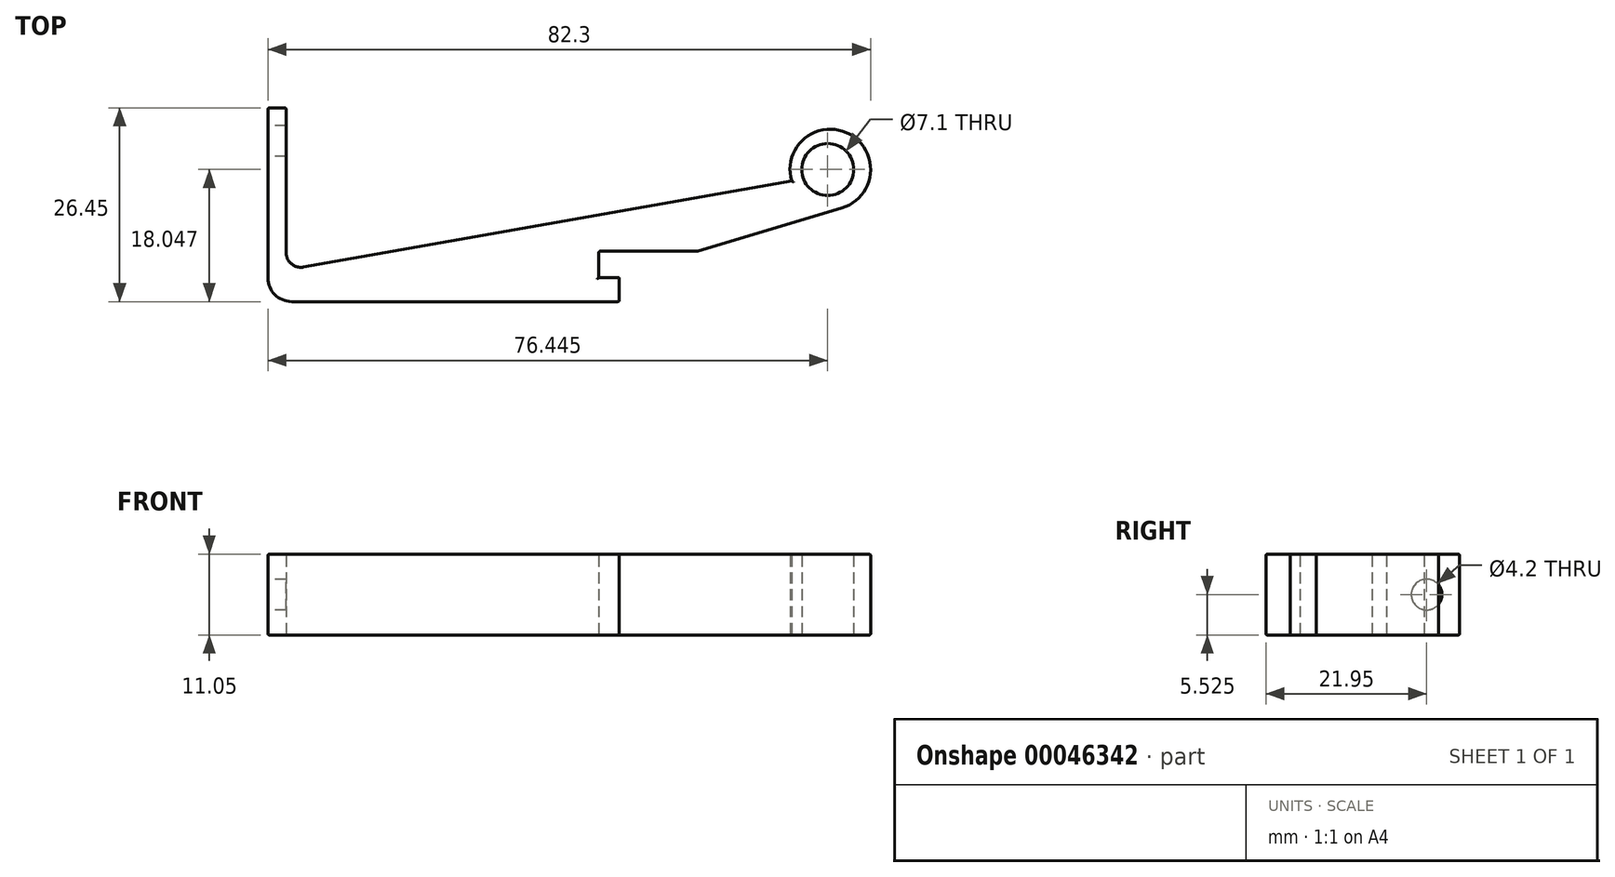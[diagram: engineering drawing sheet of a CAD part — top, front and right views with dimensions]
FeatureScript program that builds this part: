
annotation { "Feature Type Name" : "Feature", "Feature Type Description" : "" }
export const myFeature = defineFeature(function(context is Context, id is Id, definition is map)
    precondition{}
    {
        {
            var Q0;
            Q0=qCreatedBy(makeId("Top.planeOp"),FACE);
            var sketch = newSketch(context, id + "F0", { "sketchPlane" : qUnion([Q0])});
            skLineSegment(sketch, "E0.bottom", {"start": v(-32.06, 26.45) * mm, "end": v(-29.56, 26.45) * mm});
            skLineSegment(sketch, "E0.top", {"start": v(-32.06, 0) * mm, "end": v(-29.56, 0) * mm});
            skLineSegment(sketch, "E0.left", {"start": v(-32.06, 26.45) * mm, "end": v(-32.06, 0) * mm});
            skLineSegment(sketch, "E0.right", {"start": v(-29.56, 26.45) * mm, "end": v(-29.56, 4.3) * mm});
            skLineSegment(sketch, "E1", {"start": v(-29.56, 0) * mm, "end": v(15.94, 0) * mm});
            skLineSegment(sketch, "E2", {"start": v(15.94, 0) * mm, "end": v(15.94, 3.3) * mm});
            skLineSegment(sketch, "E3", {"start": v(15.94, 3.3) * mm, "end": v(13.14, 3.3) * mm});
            skLineSegment(sketch, "E4", {"start": v(13.14, 3.3) * mm, "end": v(13.14, 6.9) * mm});
            skLineSegment(sketch, "E5", {"start": v(13.14, 6.9) * mm, "end": v(26.64, 6.9) * mm});
            skLineSegment(sketch, "E6", {"start": v(26.64, 6.9) * mm, "end": v(46.32, 12.77) * mm});
            skLineSegment(sketch, "E7", {"start": v(39.47, 16.47) * mm, "end": v(-29.56, 4.3) * mm});
            skLineSegment(sketch, "E8", {"start": v(-47.11, 0) * mm, "end": v(50.52, 0) * mm, "construction": true});
            skLineSegment(sketch, "E9", {"start": v(19.89, 6.9) * mm, "end": v(93.74, 6.9) * mm, "construction": true});
            skArc(sketch, "E10", {"start": v(46.32, 12.77) * mm, "mid": v(47.36, 22.88) * mm, "end": v(39.47, 16.47) * mm});
            skCircle(sketch, "E11", {"center": v(44.39, 18.05) * mm, "radius": 3.55 * mm});
            skPoint(sketch, "E12.end.orphan", {"position": v(40.88, 17.5) * mm});
            skPoint(sketch, "E13.start.orphan", {"position": v(50.24, 18.04) * mm});
            skPoint(sketch, "E14.end.orphan", {"position": v(13.14, 11.83) * mm});
            skPoint(sketch, "E15.end.orphan", {"position": v(26.64, 14.2) * mm});
            skPoint(sketch, "E16.orphan", {"position": v(53.1, 18.05) * mm});
            skPoint(sketch, "E17.orphan", {"position": v(44.39, 24.3) * mm});
            skPoint(sketch, "E18.end.orphan", {"position": v(44.39, 21.6) * mm});
            skPoint(sketch, "E18.start.orphan", {"position": v(44.39, 23.53) * mm});
            skPoint(sketch, "E19.end.orphan", {"position": v(47.94, 18.05) * mm});
            skPoint(sketch, "E20.trimOffspring.end.orphan", {"position": v(39.24, 18.05) * mm});
            skPoint(sketch, "E20.trimOffspring.start.orphan", {"position": v(40.84, 18.05) * mm});
            skPoint(sketch, "E21.trimOffspring.end.orphan", {"position": v(44.39, 12.2) * mm});
            skPoint(sketch, "E21.trimOffspring.start.orphan", {"position": v(44.39, 14.5) * mm});
            skSolve(sketch);
        }
        {
            var Q0;
            Q0=makeQuery(id+"F0.imprint","IMPRINT",FACE,{"disambiguationData":[TD([[makeQuery(id+"F0.imprint","IMPRINT",EDGE,{"derivedFrom":sQuery(id+"F0.wireOp",EDGE,"E0.bottom")}),-1.0]])]});
            extrude(context, id + "F1", {"entities" : qUnion([Q0]), "depth" : 11.05 * mm});
        }
        {
            var Q0;
            Q0=makeQuery(id+"F1.opExtrude","SWEPT_EDGE",EDGE,{"disambiguationData":[OSD([sQuery(id+"F0.wireOp",EDGE,"E0.top"),sQuery(id+"F0.wireOp",EDGE,"E0.left")])]});
            fillet(context, id + "F2", {"entities" : qUnion([Q0]), "radius" : 3.25 * mm, "tangentPropagation" : true, "allowEdgeOverflow" : false});
        }
        {
            var Q0;
            Q0=makeQuery(id+"F1.opExtrude","SWEPT_EDGE",EDGE,{"disambiguationData":[OSD([sQuery(id+"F0.wireOp",EDGE,"E0.right"),sQuery(id+"F0.wireOp",EDGE,"E7")])]});
            fillet(context, id + "F3", {"entities" : qUnion([Q0]), "radius" : 2 * mm, "tangentPropagation" : true, "allowEdgeOverflow" : false});
        }
        {
            var Q0;
            Q0=makeQuery(id+"F1.opExtrude","CAP_EDGE",EDGE,{"disambiguationData":[OSD([sQuery(id+"F0.wireOp",EDGE,"E7")])],"isStart":true});
            var Q1;
            Q1=makeQuery(id+"F1.opExtrude","CAP_EDGE",EDGE,{"disambiguationData":[OSD([sQuery(id+"F0.wireOp",EDGE,"E10")])],"isStart":true});
            var Q2;
            Q2=makeQuery(id+"F1.opExtrude","CAP_EDGE",EDGE,{"disambiguationData":[OSD([sQuery(id+"F0.wireOp",EDGE,"E6")])],"isStart":true});
            var Q3;
            Q3=makeQuery(id+"F1.opExtrude","CAP_EDGE",EDGE,{"disambiguationData":[OSD([sQuery(id+"F0.wireOp",EDGE,"E5")])],"isStart":true});
            var Q4;
            Q4=makeQuery(id+"F1.opExtrude","CAP_EDGE",EDGE,{"disambiguationData":[OSD([sQuery(id+"F0.wireOp",EDGE,"E4")])],"isStart":true});
            var Q5;
            Q5=makeQuery(id+"F1.opExtrude","CAP_EDGE",EDGE,{"disambiguationData":[OSD([sQuery(id+"F0.wireOp",EDGE,"E3")])],"isStart":true});
            var Q6;
            Q6=makeQuery(id+"F1.opExtrude","CAP_EDGE",EDGE,{"disambiguationData":[OSD([sQuery(id+"F0.wireOp",EDGE,"E0.top"),sQuery(id+"F0.wireOp",EDGE,"E1")])],"isStart":true});
            var Q7;
            Q7=makeQuery(id+"F1.opExtrude","CAP_EDGE",EDGE,{"disambiguationData":[OSD([sQuery(id+"F0.wireOp",EDGE,"E2")])],"isStart":true});
            var Q8;
            {var subQ0=sQuery(id+"F0.wireOp",EDGE,"E0.top");var subQ1=sQuery(id+"F0.wireOp",EDGE,"E0.left");Q8=makeQuery(id+"F2.opFillet","BLEND_EDGE",EDGE,{"blendedFrom":[makeQuery(id+"F1.opExtrude","SWEPT_EDGE",EDGE,{"disambiguationData":[OSD([subQ0,subQ1])]}),makeQuery(id+"F1.opExtrude","CAP_FACE",FACE,{"disambiguationData":[OSD([sQuery(id+"F0.wireOp",EDGE,"E0.bottom"),subQ0,subQ1,sQuery(id+"F0.wireOp",EDGE,"E0.right"),sQuery(id+"F0.wireOp",EDGE,"E1"),sQuery(id+"F0.wireOp",EDGE,"E2"),sQuery(id+"F0.wireOp",EDGE,"E3"),sQuery(id+"F0.wireOp",EDGE,"E4"),sQuery(id+"F0.wireOp",EDGE,"E5"),sQuery(id+"F0.wireOp",EDGE,"E6"),sQuery(id+"F0.wireOp",EDGE,"E7"),sQuery(id+"F0.wireOp",EDGE,"E10"),sQuery(id+"F0.wireOp",EDGE,"E11")])],"isStart":true})],"blendedInto":[makeQuery(id+"F1.opExtrude","CAP_FACE",FACE,{"disambiguationData":[OSD([sQuery(id+"F0.wireOp",EDGE,"E0.bottom"),subQ0,subQ1,sQuery(id+"F0.wireOp",EDGE,"E0.right"),sQuery(id+"F0.wireOp",EDGE,"E1"),sQuery(id+"F0.wireOp",EDGE,"E2"),sQuery(id+"F0.wireOp",EDGE,"E3"),sQuery(id+"F0.wireOp",EDGE,"E4"),sQuery(id+"F0.wireOp",EDGE,"E5"),sQuery(id+"F0.wireOp",EDGE,"E6"),sQuery(id+"F0.wireOp",EDGE,"E7"),sQuery(id+"F0.wireOp",EDGE,"E10"),sQuery(id+"F0.wireOp",EDGE,"E11")])],"isStart":true})]});}
            var Q9;
            {var subQ0=sQuery(id+"F0.wireOp",EDGE,"E0.right");var subQ1=sQuery(id+"F0.wireOp",EDGE,"E7");Q9=makeQuery(id+"F3.opFillet","BLEND_EDGE",EDGE,{"blendedFrom":[makeQuery(id+"F1.opExtrude","SWEPT_EDGE",EDGE,{"disambiguationData":[OSD([subQ0,subQ1])]}),makeQuery(id+"F1.opExtrude","CAP_FACE",FACE,{"disambiguationData":[OSD([sQuery(id+"F0.wireOp",EDGE,"E0.bottom"),sQuery(id+"F0.wireOp",EDGE,"E0.top"),sQuery(id+"F0.wireOp",EDGE,"E0.left"),subQ0,sQuery(id+"F0.wireOp",EDGE,"E1"),sQuery(id+"F0.wireOp",EDGE,"E2"),sQuery(id+"F0.wireOp",EDGE,"E3"),sQuery(id+"F0.wireOp",EDGE,"E4"),sQuery(id+"F0.wireOp",EDGE,"E5"),sQuery(id+"F0.wireOp",EDGE,"E6"),subQ1,sQuery(id+"F0.wireOp",EDGE,"E10"),sQuery(id+"F0.wireOp",EDGE,"E11")])],"isStart":true})],"blendedInto":[makeQuery(id+"F1.opExtrude","CAP_FACE",FACE,{"disambiguationData":[OSD([sQuery(id+"F0.wireOp",EDGE,"E0.bottom"),sQuery(id+"F0.wireOp",EDGE,"E0.top"),sQuery(id+"F0.wireOp",EDGE,"E0.left"),subQ0,sQuery(id+"F0.wireOp",EDGE,"E1"),sQuery(id+"F0.wireOp",EDGE,"E2"),sQuery(id+"F0.wireOp",EDGE,"E3"),sQuery(id+"F0.wireOp",EDGE,"E4"),sQuery(id+"F0.wireOp",EDGE,"E5"),sQuery(id+"F0.wireOp",EDGE,"E6"),subQ1,sQuery(id+"F0.wireOp",EDGE,"E10"),sQuery(id+"F0.wireOp",EDGE,"E11")])],"isStart":true})]});}
            var Q10;
            Q10=makeQuery(id+"F1.opExtrude","CAP_EDGE",EDGE,{"disambiguationData":[OSD([sQuery(id+"F0.wireOp",EDGE,"E0.right")])],"isStart":true});
            var Q11;
            Q11=makeQuery(id+"F1.opExtrude","CAP_EDGE",EDGE,{"disambiguationData":[OSD([sQuery(id+"F0.wireOp",EDGE,"E0.left")])],"isStart":true});
            var Q12;
            Q12=makeQuery(id+"F1.opExtrude","SWEPT_EDGE",EDGE,{"disambiguationData":[OSD([sQuery(id+"F0.wireOp",EDGE,"E0.bottom"),sQuery(id+"F0.wireOp",EDGE,"E0.left")])]});
            var Q13;
            Q13=makeQuery(id+"F1.opExtrude","SWEPT_EDGE",EDGE,{"disambiguationData":[OSD([sQuery(id+"F0.wireOp",EDGE,"E0.bottom"),sQuery(id+"F0.wireOp",EDGE,"E0.right")])]});
            var Q14;
            Q14=makeQuery(id+"F1.opExtrude","CAP_EDGE",EDGE,{"disambiguationData":[OSD([sQuery(id+"F0.wireOp",EDGE,"E0.bottom")])],"isStart":false});
            var Q15;
            Q15=makeQuery(id+"F1.opExtrude","CAP_EDGE",EDGE,{"disambiguationData":[OSD([sQuery(id+"F0.wireOp",EDGE,"E0.left")])],"isStart":false});
            var Q16;
            Q16=makeQuery(id+"F1.opExtrude","CAP_EDGE",EDGE,{"disambiguationData":[OSD([sQuery(id+"F0.wireOp",EDGE,"E0.right")])],"isStart":false});
            var Q17;
            {var subQ0=sQuery(id+"F0.wireOp",EDGE,"E0.top");var subQ1=sQuery(id+"F0.wireOp",EDGE,"E0.left");Q17=makeQuery(id+"F2.opFillet","BLEND_EDGE",EDGE,{"blendedFrom":[makeQuery(id+"F1.opExtrude","SWEPT_EDGE",EDGE,{"disambiguationData":[OSD([subQ0,subQ1])]}),makeQuery(id+"F1.opExtrude","CAP_FACE",FACE,{"disambiguationData":[OSD([sQuery(id+"F0.wireOp",EDGE,"E0.bottom"),subQ0,subQ1,sQuery(id+"F0.wireOp",EDGE,"E0.right"),sQuery(id+"F0.wireOp",EDGE,"E1"),sQuery(id+"F0.wireOp",EDGE,"E2"),sQuery(id+"F0.wireOp",EDGE,"E3"),sQuery(id+"F0.wireOp",EDGE,"E4"),sQuery(id+"F0.wireOp",EDGE,"E5"),sQuery(id+"F0.wireOp",EDGE,"E6"),sQuery(id+"F0.wireOp",EDGE,"E7"),sQuery(id+"F0.wireOp",EDGE,"E10"),sQuery(id+"F0.wireOp",EDGE,"E11")])],"isStart":false})],"blendedInto":[makeQuery(id+"F1.opExtrude","CAP_FACE",FACE,{"disambiguationData":[OSD([sQuery(id+"F0.wireOp",EDGE,"E0.bottom"),subQ0,subQ1,sQuery(id+"F0.wireOp",EDGE,"E0.right"),sQuery(id+"F0.wireOp",EDGE,"E1"),sQuery(id+"F0.wireOp",EDGE,"E2"),sQuery(id+"F0.wireOp",EDGE,"E3"),sQuery(id+"F0.wireOp",EDGE,"E4"),sQuery(id+"F0.wireOp",EDGE,"E5"),sQuery(id+"F0.wireOp",EDGE,"E6"),sQuery(id+"F0.wireOp",EDGE,"E7"),sQuery(id+"F0.wireOp",EDGE,"E10"),sQuery(id+"F0.wireOp",EDGE,"E11")])],"isStart":false})]});}
            var Q18;
            {var subQ0=sQuery(id+"F0.wireOp",EDGE,"E0.right");var subQ1=sQuery(id+"F0.wireOp",EDGE,"E7");Q18=makeQuery(id+"F3.opFillet","BLEND_EDGE",EDGE,{"blendedFrom":[makeQuery(id+"F1.opExtrude","SWEPT_EDGE",EDGE,{"disambiguationData":[OSD([subQ0,subQ1])]}),makeQuery(id+"F1.opExtrude","CAP_FACE",FACE,{"disambiguationData":[OSD([sQuery(id+"F0.wireOp",EDGE,"E0.bottom"),sQuery(id+"F0.wireOp",EDGE,"E0.top"),sQuery(id+"F0.wireOp",EDGE,"E0.left"),subQ0,sQuery(id+"F0.wireOp",EDGE,"E1"),sQuery(id+"F0.wireOp",EDGE,"E2"),sQuery(id+"F0.wireOp",EDGE,"E3"),sQuery(id+"F0.wireOp",EDGE,"E4"),sQuery(id+"F0.wireOp",EDGE,"E5"),sQuery(id+"F0.wireOp",EDGE,"E6"),subQ1,sQuery(id+"F0.wireOp",EDGE,"E10"),sQuery(id+"F0.wireOp",EDGE,"E11")])],"isStart":false})],"blendedInto":[makeQuery(id+"F1.opExtrude","CAP_FACE",FACE,{"disambiguationData":[OSD([sQuery(id+"F0.wireOp",EDGE,"E0.bottom"),sQuery(id+"F0.wireOp",EDGE,"E0.top"),sQuery(id+"F0.wireOp",EDGE,"E0.left"),subQ0,sQuery(id+"F0.wireOp",EDGE,"E1"),sQuery(id+"F0.wireOp",EDGE,"E2"),sQuery(id+"F0.wireOp",EDGE,"E3"),sQuery(id+"F0.wireOp",EDGE,"E4"),sQuery(id+"F0.wireOp",EDGE,"E5"),sQuery(id+"F0.wireOp",EDGE,"E6"),subQ1,sQuery(id+"F0.wireOp",EDGE,"E10"),sQuery(id+"F0.wireOp",EDGE,"E11")])],"isStart":false})]});}
            var Q19;
            Q19=makeQuery(id+"F1.opExtrude","CAP_EDGE",EDGE,{"disambiguationData":[OSD([sQuery(id+"F0.wireOp",EDGE,"E0.top"),sQuery(id+"F0.wireOp",EDGE,"E1")])],"isStart":false});
            var Q20;
            Q20=makeQuery(id+"F1.opExtrude","CAP_EDGE",EDGE,{"disambiguationData":[OSD([sQuery(id+"F0.wireOp",EDGE,"E7")])],"isStart":false});
            var Q21;
            Q21=makeQuery(id+"F1.opExtrude","CAP_EDGE",EDGE,{"disambiguationData":[OSD([sQuery(id+"F0.wireOp",EDGE,"E2")])],"isStart":false});
            var Q22;
            Q22=makeQuery(id+"F1.opExtrude","CAP_EDGE",EDGE,{"disambiguationData":[OSD([sQuery(id+"F0.wireOp",EDGE,"E5")])],"isStart":false});
            var Q23;
            Q23=makeQuery(id+"F1.opExtrude","CAP_EDGE",EDGE,{"disambiguationData":[OSD([sQuery(id+"F0.wireOp",EDGE,"E6")])],"isStart":false});
            var Q24;
            Q24=makeQuery(id+"F1.opExtrude","CAP_EDGE",EDGE,{"disambiguationData":[OSD([sQuery(id+"F0.wireOp",EDGE,"E10")])],"isStart":false});
            var Q25;
            Q25=makeQuery(id+"F1.opExtrude","CAP_EDGE",EDGE,{"disambiguationData":[OSD([sQuery(id+"F0.wireOp",EDGE,"E3")])],"isStart":false});
            var Q26;
            Q26=makeQuery(id+"F1.opExtrude","SWEPT_EDGE",EDGE,{"disambiguationData":[OSD([sQuery(id+"F0.wireOp",EDGE,"E2"),sQuery(id+"F0.wireOp",EDGE,"E3")])]});
            var Q27;
            Q27=makeQuery(id+"F1.opExtrude","CAP_EDGE",EDGE,{"disambiguationData":[OSD([sQuery(id+"F0.wireOp",EDGE,"E4")])],"isStart":false});
            var Q28;
            Q28=makeQuery(id+"F1.opExtrude","SWEPT_EDGE",EDGE,{"disambiguationData":[OSD([sQuery(id+"F0.wireOp",EDGE,"E4"),sQuery(id+"F0.wireOp",EDGE,"E5")])]});
            var Q29;
            Q29=makeQuery(id+"F1.opExtrude","SWEPT_EDGE",EDGE,{"disambiguationData":[OSD([sQuery(id+"F0.wireOp",EDGE,"E1"),sQuery(id+"F0.wireOp",EDGE,"E2")])]});
            var Q30;
            Q30=makeQuery(id+"F1.opExtrude","SWEPT_EDGE",EDGE,{"disambiguationData":[OSD([sQuery(id+"F0.wireOp",EDGE,"E5"),sQuery(id+"F0.wireOp",EDGE,"E6")])]});
            var Q31;
            Q31=makeQuery(id+"F1.opExtrude","CAP_EDGE",EDGE,{"disambiguationData":[OSD([sQuery(id+"F0.wireOp",EDGE,"E11")])],"isStart":false});
            var Q32;
            Q32=makeQuery(id+"F1.opExtrude","CAP_EDGE",EDGE,{"disambiguationData":[OSD([sQuery(id+"F0.wireOp",EDGE,"E11")])],"isStart":true});
            var Q33;
            Q33=makeQuery(id+"F1.opExtrude","CAP_EDGE",EDGE,{"disambiguationData":[OSD([sQuery(id+"F0.wireOp",EDGE,"E0.bottom")])],"isStart":true});
            fillet(context, id + "F4", {"entities" : qUnion([Q0, Q1, Q2, Q3, Q4, Q5, Q6, Q7, Q8, Q9, Q10, Q11, Q12, Q13, Q14, Q15, Q16, Q17, Q18, Q19, Q20, Q21, Q22, Q23, Q24, Q25, Q26, Q27, Q28, Q29, Q30, Q31, Q32, Q33]), "radius" : 0.2 * mm, "tangentPropagation" : true, "allowEdgeOverflow" : false});
        }
        {
            var Q0;
            Q0=makeQuery(id+"F1.opExtrude","SWEPT_FACE",FACE,{"disambiguationData":[OSD([sQuery(id+"F0.wireOp",EDGE,"E0.left")])]});
            var sketch = newSketch(context, id + "F5", { "sketchPlane" : qUnion([Q0])});
            skCircle(sketch, "E22", {"center": v(-21.95, 5.53) * mm, "radius": 2.1 * mm});
            skLineSegment(sketch, "E23", {"start": v(-24.48, 0) * mm, "end": v(-2.12, 0) * mm, "construction": true});
            skLineSegment(sketch, "E24", {"start": v(-34.74, 0) * mm, "end": v(2.18, 0) * mm, "construction": true});
            skLineSegment(sketch, "E25", {"start": v(0, 11.05) * mm, "end": v(-36.1, 11.05) * mm, "construction": true});
            skSolve(sketch);
        }
        {
            var Q0;
            Q0=makeQuery(id+"F5.imprint","IMPRINT",FACE,{"disambiguationData":[TD([[makeQuery(id+"F5.imprint","IMPRINT",EDGE,{"derivedFrom":sQuery(id+"F5.wireOp",EDGE,"E22")}),1.0]])]});
            extrude(context, id + "F6", {"entities" : qUnion([Q0]), "operationType" : NewBodyOperationType.REMOVE, "endBound" : BoundingType.SYMMETRIC, "oppositeDirection" : true, "depth" : 25 * mm});
        }
    });
